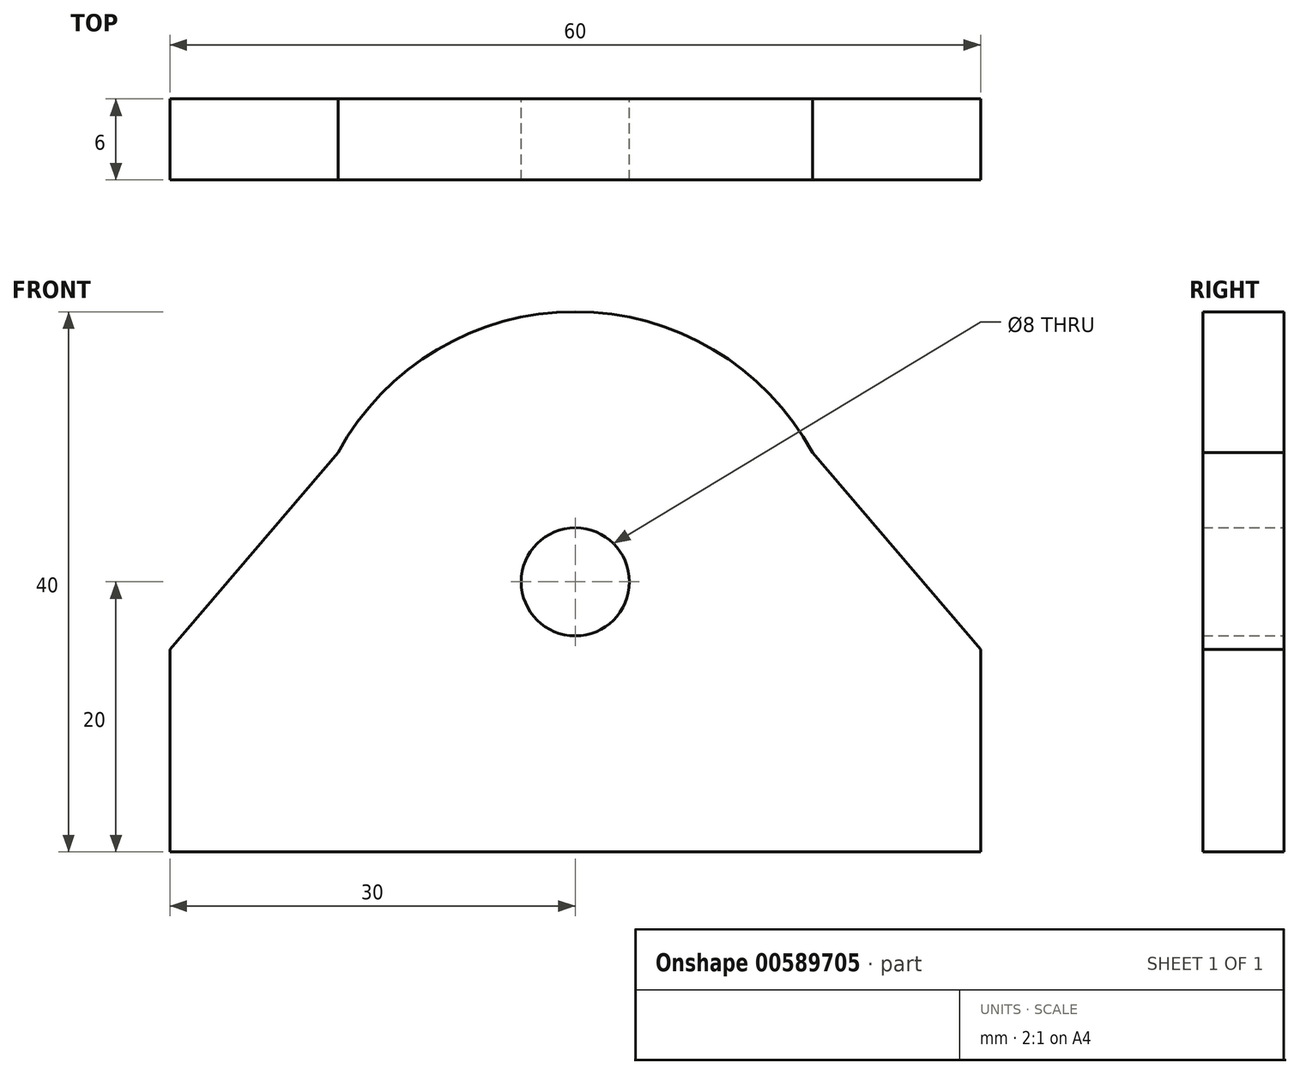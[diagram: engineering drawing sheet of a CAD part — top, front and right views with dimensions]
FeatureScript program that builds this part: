
annotation { "Feature Type Name" : "Feature", "Feature Type Description" : "" }
export const myFeature = defineFeature(function(context is Context, id is Id, definition is map)
    precondition{}
    {
        {
            var Q0;
            Q0=qCreatedBy(makeId("Front.planeOp"),FACE);
            var sketch = newSketch(context, id + "F0", { "sketchPlane" : qUnion([Q0])});
            skLineSegment(sketch, "E0.bottom", {"start": v(0, 0) * mm, "end": v(-30, 0) * mm});
            skLineSegment(sketch, "E0.left", {"start": v(0, 0) * mm, "end": v(0, 20) * mm, "construction": true});
            skArc(sketch, "E1", {"start": v(0, 40) * mm, "mid": v(-10.22, 37.2) * mm, "end": v(-17.56, 29.56) * mm});
            skArc(sketch, "E2.MirrorCS", {"start": v(0, 40) * mm, "mid": v(10.22, 37.2) * mm, "end": v(17.56, 29.56) * mm});
            skCircle(sketch, "E3", {"center": v(0, 20) * mm, "radius": 4 * mm});
            skLineSegment(sketch, "E4", {"start": v(-30, 0) * mm, "end": v(-30, 15) * mm});
            skLineSegment(sketch, "E5", {"start": v(-30, 15) * mm, "end": v(-17.56, 29.56) * mm});
            skLineSegment(sketch, "E6.MirrorCS", {"start": v(0, 0) * mm, "end": v(30, 0) * mm});
            skLineSegment(sketch, "E7.MirrorCS", {"start": v(30, 0) * mm, "end": v(30, 15) * mm});
            skLineSegment(sketch, "E8.MirrorCS", {"start": v(30, 15) * mm, "end": v(17.56, 29.56) * mm});
            skSolve(sketch);
        }
        {
            var Q0;
            Q0 = qSketchRegion(id + "F0", true);
            extrude(context, id + "F1", {"entities" : qUnion([Q0]), "depth" : 6 * mm, "offsetDistance" : 25 * mm});
        }
    });
